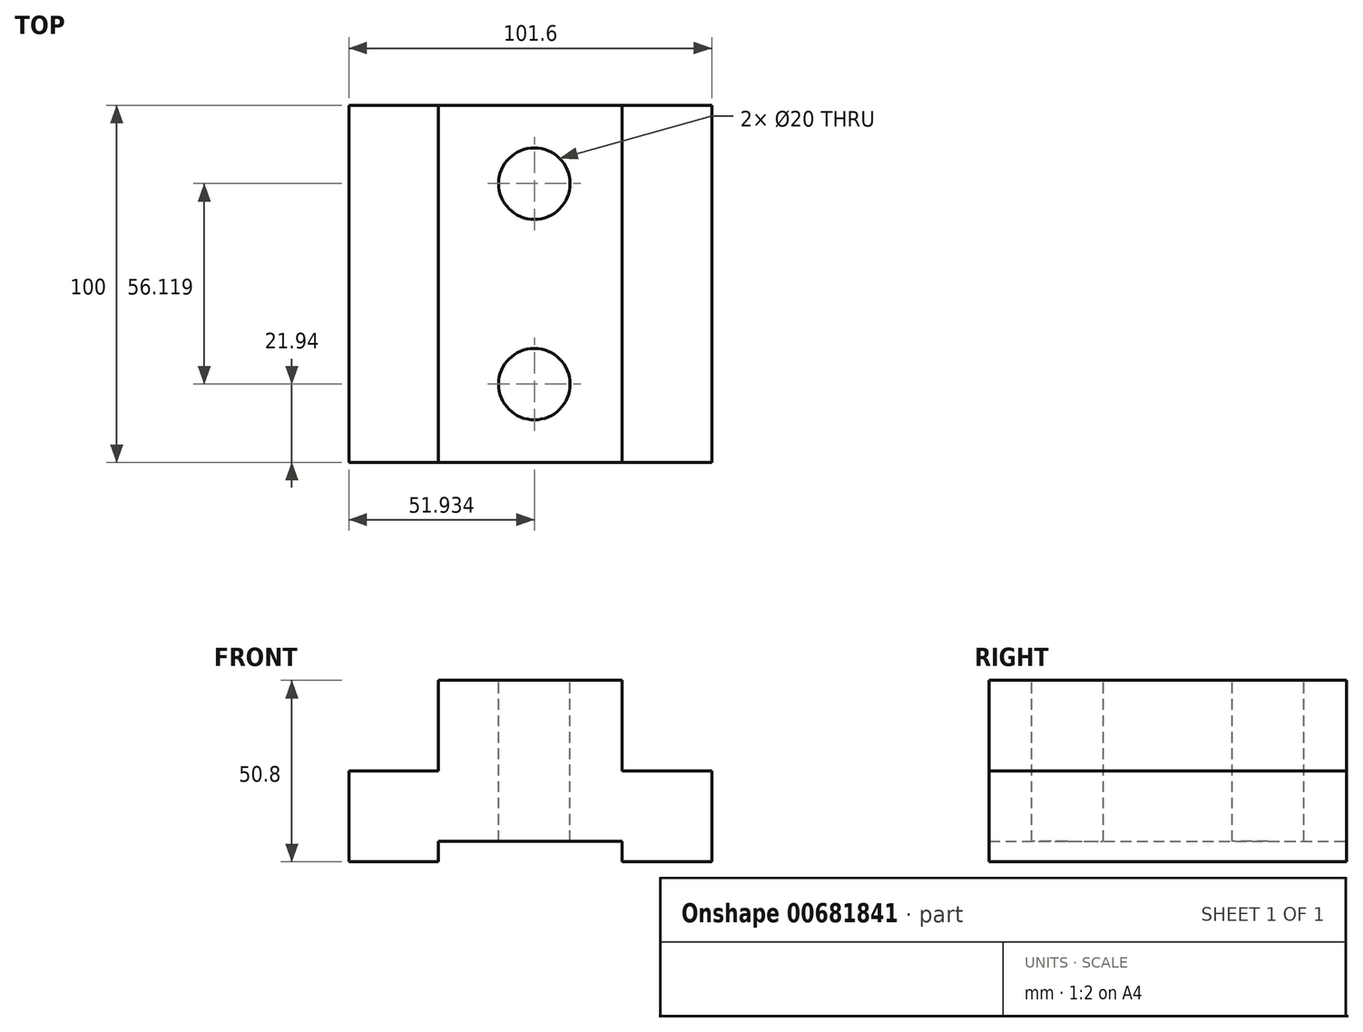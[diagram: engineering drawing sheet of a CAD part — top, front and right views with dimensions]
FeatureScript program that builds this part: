
annotation { "Feature Type Name" : "Feature", "Feature Type Description" : "" }
export const myFeature = defineFeature(function(context is Context, id is Id, definition is map)
    precondition{}
    {
        {
            var Q0;
            Q0=qCreatedBy(makeId("Front.planeOp"),FACE);
            var sketch = newSketch(context, id + "F0", { "sketchPlane" : qUnion([Q0])});
            skLineSegment(sketch, "E0", {"start": v(-17.15, 22.62) * mm, "end": v(-17.15, -2.78) * mm});
            skLineSegment(sketch, "E1", {"start": v(-17.15, -2.78) * mm, "end": v(7.93, -2.78) * mm});
            skLineSegment(sketch, "E2", {"start": v(7.93, -2.78) * mm, "end": v(7.93, -28.18) * mm});
            skLineSegment(sketch, "E3", {"start": v(7.93, -28.18) * mm, "end": v(-17.15, -28.18) * mm});
            skLineSegment(sketch, "E4", {"start": v(-17.15, -28.18) * mm, "end": v(-17.15, -22.4) * mm});
            skLineSegment(sketch, "E5", {"start": v(-17.15, -22.4) * mm, "end": v(-42.87, -22.4) * mm});
            skLineSegment(sketch, "E6", {"start": v(-42.87, -22.4) * mm, "end": v(-42.87, 22.62) * mm});
            skLineSegment(sketch, "E7", {"start": v(-42.87, 22.62) * mm, "end": v(-17.15, 22.62) * mm});
            skLineSegment(sketch, "E8.MirrorCS", {"start": v(-42.87, 22.62) * mm, "end": v(-68.6, 22.62) * mm});
            skLineSegment(sketch, "E9.MirrorCS", {"start": v(-68.6, 22.62) * mm, "end": v(-68.6, -2.78) * mm});
            skLineSegment(sketch, "E10.MirrorCS", {"start": v(-68.6, -2.78) * mm, "end": v(-93.67, -2.78) * mm});
            skLineSegment(sketch, "E11.MirrorCS", {"start": v(-93.67, -2.78) * mm, "end": v(-93.67, -28.18) * mm});
            skLineSegment(sketch, "E12.MirrorCS", {"start": v(-93.67, -28.18) * mm, "end": v(-68.6, -28.18) * mm});
            skLineSegment(sketch, "E13.MirrorCS", {"start": v(-68.6, -22.4) * mm, "end": v(-42.87, -22.4) * mm});
            skLineSegment(sketch, "E14.MirrorCS", {"start": v(-68.6, -28.18) * mm, "end": v(-68.6, -22.4) * mm});
            skSolve(sketch);
        }
        {
            var Q0;
            Q0 = qSketchRegion(id + "F0", true);
            extrude(context, id + "F1", {"entities" : qUnion([Q0]), "depth" : 100 * mm, "offsetDistance" : 25.4 * mm});
        }
        {
            var Q0;
            Q0=makeQuery(id+"F1.opExtrude","SWEPT_FACE",FACE,{"disambiguationData":[OSD([sQuery(id+"F0.wireOp",EDGE,"E7"),sQuery(id+"F0.wireOp",EDGE,"E8.MirrorCS")])]});
            var sketch = newSketch(context, id + "F2", { "sketchPlane" : qUnion([Q0])});
            skCircle(sketch, "E15", {"center": v(-41.74, -21.94) * mm, "radius": 10.59 * mm});
            skLineSegment(sketch, "E16", {"start": v(-68.6, 0) * mm, "end": v(-17.15, 0) * mm});
            skLineSegment(sketch, "E17", {"start": v(-68.6, -50) * mm, "end": v(-17.15, -50) * mm});
            skCircle(sketch, "E18.MirrorC", {"center": v(-41.74, -78.06) * mm, "radius": 10.59 * mm});
            skSolve(sketch);
        }
        {
            var Q0;
            Q0=sQuery(id+"F2.wireOp",VERTEX,"E15.center");
            var Q1;
            Q1=sQuery(id+"F2.wireOp",VERTEX,"E18.MirrorC.center");
            var Q2;
            Q2=makeQuery(id+"F1.opExtrude","SWEPT_BODY",BODY,{"disambiguationData":[OSD([sQuery(id+"F0.wireOp",EDGE,"E0"),sQuery(id+"F0.wireOp",EDGE,"E1"),sQuery(id+"F0.wireOp",EDGE,"E2"),sQuery(id+"F0.wireOp",EDGE,"E3"),sQuery(id+"F0.wireOp",EDGE,"E4"),sQuery(id+"F0.wireOp",EDGE,"E5"),sQuery(id+"F0.wireOp",EDGE,"E7"),sQuery(id+"F0.wireOp",EDGE,"E8.MirrorCS"),sQuery(id+"F0.wireOp",EDGE,"E9.MirrorCS"),sQuery(id+"F0.wireOp",EDGE,"E10.MirrorCS"),sQuery(id+"F0.wireOp",EDGE,"E11.MirrorCS"),sQuery(id+"F0.wireOp",EDGE,"E12.MirrorCS"),sQuery(id+"F0.wireOp",EDGE,"E13.MirrorCS"),sQuery(id+"F0.wireOp",EDGE,"E14.MirrorCS")])]});
            hole(context, id + "F3", {"style" : HoleStyle.SIMPLE, "endStyle" : HoleEndStyle.THROUGH, "holeDiameter" : 20 * mm, "majorDiameter" : 5 * mm, "isTappedThrough" : true, "tappedDepth" : 12 * mm, "tapClearance" : 3, "locations" : qUnion([Q0, Q1]), "scope" : qUnion([Q2])});
        }
    });
